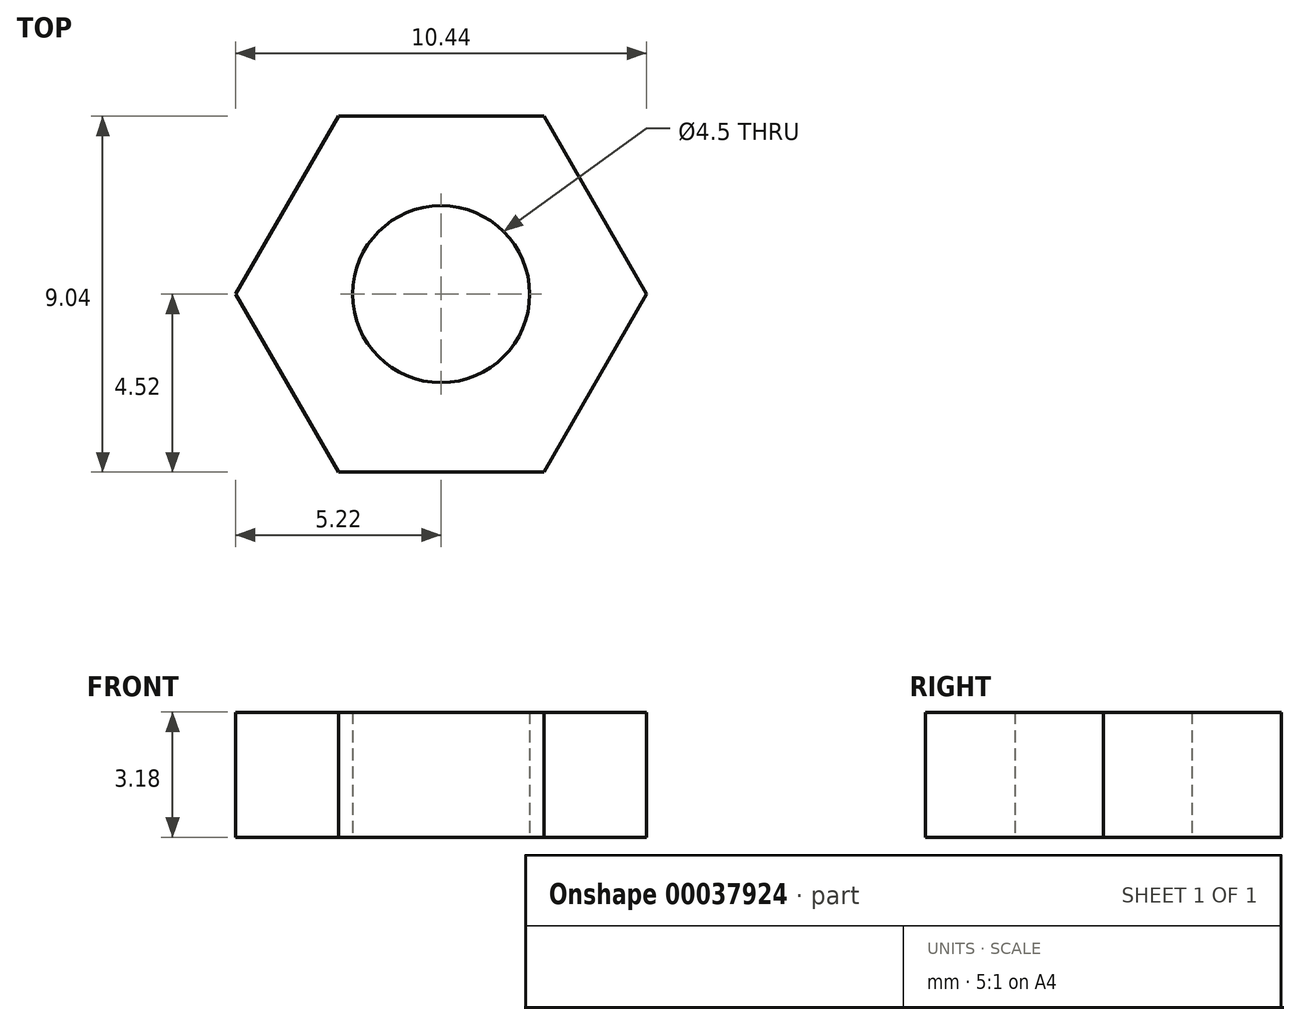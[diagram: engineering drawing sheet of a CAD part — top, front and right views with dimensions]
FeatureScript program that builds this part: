
annotation { "Feature Type Name" : "Feature", "Feature Type Description" : "" }
export const myFeature = defineFeature(function(context is Context, id is Id, definition is map)
    precondition{}
    {
        {
            var Q0;
            Q0=qCreatedBy(makeId("Top.planeOp"),FACE);
            var sketch = newSketch(context, id + "F0", { "sketchPlane" : qUnion([Q0])});
            skCircle(sketch, "E0", {"center": v(0, 0) * mm, "radius": 2.25 * mm});
            skCircle(sketch, "E1.cCircle", {"center": v(0, 0) * mm, "radius": 4.52 * mm, "construction": true});
            skLineSegment(sketch, "E1.0", {"start": v(5.22, 0) * mm, "end": v(2.61, -4.52) * mm});
            skLineSegment(sketch, "E1.1", {"start": v(2.61, -4.52) * mm, "end": v(-2.61, -4.52) * mm});
            skLineSegment(sketch, "E1.2", {"start": v(-2.61, -4.52) * mm, "end": v(-5.22, 0) * mm});
            skLineSegment(sketch, "E1.3", {"start": v(-5.22, 0) * mm, "end": v(-2.61, 4.52) * mm});
            skLineSegment(sketch, "E1.4", {"start": v(-2.61, 4.52) * mm, "end": v(2.61, 4.52) * mm});
            skLineSegment(sketch, "E1.5", {"start": v(2.61, 4.52) * mm, "end": v(5.22, 0) * mm});
            skPoint(sketch, "E1.0.midPoint", {"position": v(3.92, -2.26) * mm});
            skSolve(sketch);
        }
        {
            var Q0;
            Q0 = qSketchRegion(id + "F0", true);
            extrude(context, id + "F1", {"entities" : qUnion([Q0]), "depth" : 3.17 * mm});
        }
    });
